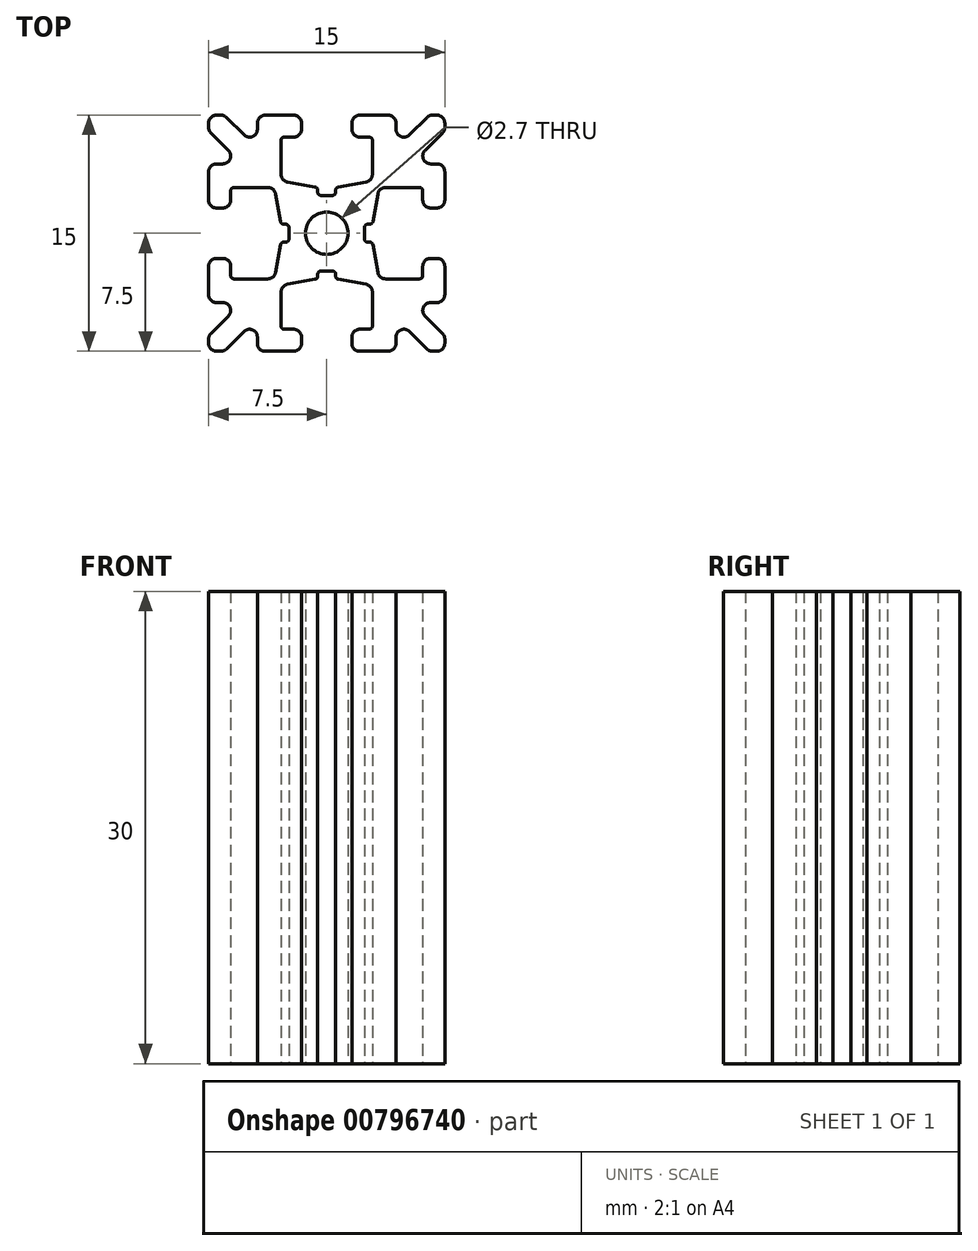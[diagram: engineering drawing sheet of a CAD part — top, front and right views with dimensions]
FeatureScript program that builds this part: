
annotation { "Feature Type Name" : "Feature", "Feature Type Description" : "" }
export const myFeature = defineFeature(function(context is Context, id is Id, definition is map)
    precondition{}
    {
        {
            var Q0;
            Q0=qCreatedBy(makeId("Top.planeOp"),FACE);
            var sketch = newSketch(context, id + "F0", { "sketchPlane" : qUnion([Q0])});
            skLineSegment(sketch, "E0", {"start": v(0, 0) * mm, "end": v(-7.5, -7.5) * mm, "construction": true});
            skArc(sketch, "E1", {"start": v(-1.35, 0) * mm, "mid": v(-1.25, -0.52) * mm, "end": v(-0.95, -0.95) * mm});
            skLineSegment(sketch, "E2", {"start": v(-7.5, -7) * mm, "end": v(-7.5, -6.72) * mm});
            skLineSegment(sketch, "E3", {"start": v(-7.35, -6.36) * mm, "end": v(-6.25, -5.26) * mm});
            skLineSegment(sketch, "E4", {"start": v(-6.6, -4.4) * mm, "end": v(-7, -4.4) * mm});
            skLineSegment(sketch, "E5", {"start": v(-7.5, -3.9) * mm, "end": v(-7.5, -2.1) * mm});
            skLineSegment(sketch, "E6", {"start": v(-7, -1.6) * mm, "end": v(-6.6, -1.6) * mm});
            skLineSegment(sketch, "E7", {"start": v(-6.1, -2.1) * mm, "end": v(-6.1, -2.7) * mm});
            skLineSegment(sketch, "E8", {"start": v(-5.9, -2.9) * mm, "end": v(-3.74, -2.9) * mm});
            skLineSegment(sketch, "E9", {"start": v(-3.25, -2.49) * mm, "end": v(-2.93, -0.73) * mm});
            skLineSegment(sketch, "E10", {"start": v(-2.73, -0.57) * mm, "end": v(-2.6, -0.57) * mm});
            skLineSegment(sketch, "E11", {"start": v(-2.4, -0.37) * mm, "end": v(-2.4, 0) * mm});
            skLineSegment(sketch, "E12", {"start": v(-2.4, 0) * mm, "end": v(-1.35, 0) * mm, "construction": true});
            skPoint(sketch, "E13.visualSharp", {"position": v(-5.4, -4.4) * mm});
            skArc(sketch, "E13.filletArc", {"start": v(-6.25, -5.26) * mm, "mid": v(-6.14, -4.71) * mm, "end": v(-6.6, -4.4) * mm});
            skPoint(sketch, "E14.visualSharp", {"position": v(-6.1, -2.9) * mm});
            skArc(sketch, "E14.filletArc", {"start": v(-6.1, -2.7) * mm, "mid": v(-6.04, -2.84) * mm, "end": v(-5.9, -2.9) * mm});
            skPoint(sketch, "E15.visualSharp", {"position": v(-6.1, -1.6) * mm});
            skArc(sketch, "E15.filletArc", {"start": v(-6.1, -2.1) * mm, "mid": v(-6.25, -1.75) * mm, "end": v(-6.6, -1.6) * mm});
            skPoint(sketch, "E16.visualSharp", {"position": v(-7.5, -1.6) * mm});
            skArc(sketch, "E16.filletArc", {"start": v(-7, -1.6) * mm, "mid": v(-7.35, -1.75) * mm, "end": v(-7.5, -2.1) * mm});
            skPoint(sketch, "E17.visualSharp", {"position": v(-7.5, -4.4) * mm});
            skArc(sketch, "E17.filletArc", {"start": v(-7.5, -3.9) * mm, "mid": v(-7.35, -4.26) * mm, "end": v(-7, -4.4) * mm});
            skPoint(sketch, "E18.visualSharp", {"position": v(-7.5, -6.51) * mm});
            skArc(sketch, "E18.filletArc", {"start": v(-7.35, -6.36) * mm, "mid": v(-7.46, -6.53) * mm, "end": v(-7.5, -6.72) * mm});
            skPoint(sketch, "E19.visualSharp", {"position": v(-3.32, -2.9) * mm});
            skArc(sketch, "E19.filletArc", {"start": v(-3.74, -2.9) * mm, "mid": v(-3.42, -2.78) * mm, "end": v(-3.25, -2.49) * mm});
            skPoint(sketch, "E20.visualSharp", {"position": v(-2.9, -0.57) * mm});
            skArc(sketch, "E20.filletArc", {"start": v(-2.73, -0.57) * mm, "mid": v(-2.86, -0.62) * mm, "end": v(-2.93, -0.73) * mm});
            skPoint(sketch, "E21.visualSharp", {"position": v(-2.4, -0.57) * mm});
            skArc(sketch, "E21.filletArc", {"start": v(-2.6, -0.57) * mm, "mid": v(-2.46, -0.51) * mm, "end": v(-2.4, -0.37) * mm});
            skLineSegment(sketch, "E22.0.MirrorCS", {"start": v(0, -2.4) * mm, "end": v(0, -1.35) * mm, "construction": true});
            skPoint(sketch, "E22.1.MirrorP", {"position": v(-4.4, -7.5) * mm});
            skArc(sketch, "E22.2.MirrorCS", {"start": v(-6.36, -7.35) * mm, "mid": v(-6.53, -7.46) * mm, "end": v(-6.72, -7.5) * mm});
            skPoint(sketch, "E22.3.MirrorP", {"position": v(-1.6, -7.5) * mm});
            skArc(sketch, "E22.4.MirrorCS", {"start": v(-1.6, -7) * mm, "mid": v(-1.75, -7.35) * mm, "end": v(-2.1, -7.5) * mm});
            skArc(sketch, "E22.5.MirrorCS", {"start": v(-0.57, -2.73) * mm, "mid": v(-0.62, -2.86) * mm, "end": v(-0.73, -2.93) * mm});
            skPoint(sketch, "E22.6.MirrorP", {"position": v(-1.6, -6.1) * mm});
            skLineSegment(sketch, "E22.7.MirrorCS", {"start": v(-3.9, -7.5) * mm, "end": v(-2.1, -7.5) * mm});
            skArc(sketch, "E22.8.MirrorCS", {"start": v(-5.26, -6.25) * mm, "mid": v(-4.71, -6.14) * mm, "end": v(-4.4, -6.6) * mm});
            skPoint(sketch, "E22.9.MirrorP", {"position": v(-0.57, -2.4) * mm});
            skPoint(sketch, "E22.10.MirrorP", {"position": v(-4.4, -5.4) * mm});
            skArc(sketch, "E22.11.MirrorCS", {"start": v(-2.7, -6.1) * mm, "mid": v(-2.84, -6.04) * mm, "end": v(-2.9, -5.9) * mm});
            skPoint(sketch, "E22.12.MirrorP", {"position": v(-0.57, -2.9) * mm});
            skLineSegment(sketch, "E22.13.MirrorCS", {"start": v(-7, -7.5) * mm, "end": v(-6.72, -7.5) * mm});
            skLineSegment(sketch, "E22.14.MirrorCS", {"start": v(-1.6, -7) * mm, "end": v(-1.6, -6.6) * mm});
            skLineSegment(sketch, "E22.15.MirrorCS", {"start": v(-6.36, -7.35) * mm, "end": v(-5.26, -6.25) * mm});
            skArc(sketch, "E22.16.MirrorCS", {"start": v(-2.1, -6.1) * mm, "mid": v(-1.75, -6.25) * mm, "end": v(-1.6, -6.6) * mm});
            skLineSegment(sketch, "E22.17.MirrorCS", {"start": v(-4.4, -6.6) * mm, "end": v(-4.4, -7) * mm});
            skArc(sketch, "E22.18.MirrorCS", {"start": v(-2.9, -3.74) * mm, "mid": v(-2.78, -3.42) * mm, "end": v(-2.49, -3.25) * mm});
            skLineSegment(sketch, "E22.19.MirrorCS", {"start": v(-2.9, -5.9) * mm, "end": v(-2.9, -3.74) * mm});
            skLineSegment(sketch, "E22.20.MirrorCS", {"start": v(-2.1, -6.1) * mm, "end": v(-2.7, -6.1) * mm});
            skArc(sketch, "E22.21.MirrorCS", {"start": v(-0.57, -2.6) * mm, "mid": v(-0.51, -2.46) * mm, "end": v(-0.37, -2.4) * mm});
            skLineSegment(sketch, "E22.22.MirrorCS", {"start": v(-0.37, -2.4) * mm, "end": v(0, -2.4) * mm});
            skPoint(sketch, "E22.23.MirrorP", {"position": v(-6.51, -7.5) * mm});
            skPoint(sketch, "E22.24.MirrorP", {"position": v(-2.9, -6.1) * mm});
            skLineSegment(sketch, "E22.25.MirrorCS", {"start": v(-2.49, -3.25) * mm, "end": v(-0.73, -2.93) * mm});
            skLineSegment(sketch, "E22.26.MirrorCS", {"start": v(-0.57, -2.73) * mm, "end": v(-0.57, -2.6) * mm});
            skArc(sketch, "E22.27.MirrorCS", {"start": v(0, -1.35) * mm, "mid": v(-0.52, -1.25) * mm, "end": v(-0.95, -0.95) * mm});
            skArc(sketch, "E22.28.MirrorCS", {"start": v(-3.9, -7.5) * mm, "mid": v(-4.26, -7.35) * mm, "end": v(-4.4, -7) * mm});
            skPoint(sketch, "E22.29.MirrorP", {"position": v(-2.9, -3.32) * mm});
            skPoint(sketch, "E23.visualSharp", {"position": v(-7.5, -7.5) * mm});
            skArc(sketch, "E23.filletArc", {"start": v(-7.5, -7) * mm, "mid": v(-7.35, -7.35) * mm, "end": v(-7, -7.5) * mm});
            skLineSegment(sketch, "E24.0.MirrorCS", {"start": v(0, 2.4) * mm, "end": v(0, 1.35) * mm, "construction": true});
            skLineSegment(sketch, "E24.1.MirrorCS", {"start": v(-2.1, 6.1) * mm, "end": v(-2.7, 6.1) * mm});
            skLineSegment(sketch, "E24.2.MirrorCS", {"start": v(-7.5, 3.9) * mm, "end": v(-7.5, 2.1) * mm});
            skLineSegment(sketch, "E24.3.MirrorCS", {"start": v(-7, 1.6) * mm, "end": v(-6.6, 1.6) * mm});
            skArc(sketch, "E24.4.MirrorCS", {"start": v(-6.1, 2.1) * mm, "mid": v(-6.25, 1.75) * mm, "end": v(-6.6, 1.6) * mm});
            skPoint(sketch, "E24.5.MirrorP", {"position": v(-3.32, 2.9) * mm});
            skPoint(sketch, "E24.6.MirrorP", {"position": v(-0.57, 2.9) * mm});
            skArc(sketch, "E24.7.MirrorCS", {"start": v(-0.57, 2.6) * mm, "mid": v(-0.51, 2.46) * mm, "end": v(-0.37, 2.4) * mm});
            skArc(sketch, "E24.8.MirrorCS", {"start": v(-2.6, 0.57) * mm, "mid": v(-2.46, 0.51) * mm, "end": v(-2.4, 0.37) * mm});
            skLineSegment(sketch, "E24.9.MirrorCS", {"start": v(-0.37, 2.4) * mm, "end": v(0, 2.4) * mm});
            skArc(sketch, "E24.10.MirrorCS", {"start": v(-6.1, 2.7) * mm, "mid": v(-6.04, 2.84) * mm, "end": v(-5.9, 2.9) * mm});
            skPoint(sketch, "E24.11.MirrorP", {"position": v(-4.4, 5.4) * mm});
            skLineSegment(sketch, "E24.12.MirrorCS", {"start": v(-2.9, 5.9) * mm, "end": v(-2.9, 3.74) * mm});
            skLineSegment(sketch, "E24.13.MirrorCS", {"start": v(-7.35, 6.36) * mm, "end": v(-6.25, 5.26) * mm});
            skPoint(sketch, "E24.14.MirrorP", {"position": v(-7.5, 6.51) * mm});
            skArc(sketch, "E24.15.MirrorCS", {"start": v(-3.74, 2.9) * mm, "mid": v(-3.42, 2.78) * mm, "end": v(-3.25, 2.49) * mm});
            skArc(sketch, "E24.16.MirrorCS", {"start": v(-2.1, 6.1) * mm, "mid": v(-1.75, 6.25) * mm, "end": v(-1.6, 6.6) * mm});
            skArc(sketch, "E24.17.MirrorCS", {"start": v(-7, 1.6) * mm, "mid": v(-7.35, 1.75) * mm, "end": v(-7.5, 2.1) * mm});
            skPoint(sketch, "E24.18.MirrorP", {"position": v(-1.6, 6.1) * mm});
            skPoint(sketch, "E24.19.MirrorP", {"position": v(-7.5, 4.4) * mm});
            skLineSegment(sketch, "E24.20.MirrorCS", {"start": v(-4.4, 6.6) * mm, "end": v(-4.4, 7) * mm});
            skArc(sketch, "E24.21.MirrorCS", {"start": v(-7.5, 3.9) * mm, "mid": v(-7.35, 4.26) * mm, "end": v(-7, 4.4) * mm});
            skPoint(sketch, "E24.22.MirrorP", {"position": v(-0.57, 2.4) * mm});
            skLineSegment(sketch, "E24.23.MirrorCS", {"start": v(-5.9, 2.9) * mm, "end": v(-3.74, 2.9) * mm});
            skArc(sketch, "E24.24.MirrorCS", {"start": v(-2.9, 3.74) * mm, "mid": v(-2.78, 3.42) * mm, "end": v(-2.49, 3.25) * mm});
            skArc(sketch, "E24.25.MirrorCS", {"start": v(-7.35, 6.36) * mm, "mid": v(-7.46, 6.53) * mm, "end": v(-7.5, 6.72) * mm});
            skPoint(sketch, "E24.26.MirrorP", {"position": v(-6.1, 2.9) * mm});
            skPoint(sketch, "E24.27.MirrorP", {"position": v(-4.4, 7.5) * mm});
            skArc(sketch, "E24.28.MirrorCS", {"start": v(-5.26, 6.25) * mm, "mid": v(-4.71, 6.14) * mm, "end": v(-4.4, 6.6) * mm});
            skArc(sketch, "E24.29.MirrorCS", {"start": v(-7.5, 7) * mm, "mid": v(-7.35, 7.35) * mm, "end": v(-7, 7.5) * mm});
            skPoint(sketch, "E24.30.MirrorP", {"position": v(-6.1, 1.6) * mm});
            skPoint(sketch, "E24.31.MirrorP", {"position": v(-2.9, 3.32) * mm});
            skPoint(sketch, "E24.32.MirrorP", {"position": v(-1.6, 7.5) * mm});
            skPoint(sketch, "E24.33.MirrorP", {"position": v(-2.9, 6.1) * mm});
            skLineSegment(sketch, "E24.34.MirrorCS", {"start": v(-3.9, 7.5) * mm, "end": v(-2.1, 7.5) * mm});
            skLineSegment(sketch, "E24.35.MirrorCS", {"start": v(-7, 7.5) * mm, "end": v(-6.72, 7.5) * mm});
            skArc(sketch, "E24.36.MirrorCS", {"start": v(-3.9, 7.5) * mm, "mid": v(-4.26, 7.35) * mm, "end": v(-4.4, 7) * mm});
            skPoint(sketch, "E24.37.MirrorP", {"position": v(-7.5, 7.5) * mm});
            skLineSegment(sketch, "E24.38.MirrorCS", {"start": v(-1.6, 7) * mm, "end": v(-1.6, 6.6) * mm});
            skLineSegment(sketch, "E24.39.MirrorCS", {"start": v(-6.36, 7.35) * mm, "end": v(-5.26, 6.25) * mm});
            skPoint(sketch, "E24.40.MirrorP", {"position": v(-7.5, 1.6) * mm});
            skArc(sketch, "E24.41.MirrorCS", {"start": v(-2.7, 6.1) * mm, "mid": v(-2.84, 6.04) * mm, "end": v(-2.9, 5.9) * mm});
            skArc(sketch, "E24.42.MirrorCS", {"start": v(-6.36, 7.35) * mm, "mid": v(-6.53, 7.46) * mm, "end": v(-6.72, 7.5) * mm});
            skLineSegment(sketch, "E24.43.MirrorCS", {"start": v(-2.49, 3.25) * mm, "end": v(-0.73, 2.93) * mm});
            skPoint(sketch, "E24.44.MirrorP", {"position": v(-2.9, 0.57) * mm});
            skLineSegment(sketch, "E24.45.MirrorCS", {"start": v(-6.6, 4.4) * mm, "end": v(-7, 4.4) * mm});
            skArc(sketch, "E24.46.MirrorCS", {"start": v(-1.6, 7) * mm, "mid": v(-1.75, 7.35) * mm, "end": v(-2.1, 7.5) * mm});
            skArc(sketch, "E24.47.MirrorCS", {"start": v(-2.73, 0.57) * mm, "mid": v(-2.86, 0.62) * mm, "end": v(-2.93, 0.73) * mm});
            skArc(sketch, "E24.48.MirrorCS", {"start": v(-6.25, 5.26) * mm, "mid": v(-6.14, 4.71) * mm, "end": v(-6.6, 4.4) * mm});
            skLineSegment(sketch, "E24.49.MirrorCS", {"start": v(-0.57, 2.73) * mm, "end": v(-0.57, 2.6) * mm});
            skLineSegment(sketch, "E24.50.MirrorCS", {"start": v(-2.73, 0.57) * mm, "end": v(-2.6, 0.57) * mm});
            skArc(sketch, "E24.51.MirrorCS", {"start": v(-1.35, 0) * mm, "mid": v(-1.25, 0.52) * mm, "end": v(-0.95, 0.95) * mm});
            skPoint(sketch, "E24.52.MirrorP", {"position": v(-2.4, 0.57) * mm});
            skPoint(sketch, "E24.53.MirrorP", {"position": v(-5.4, 4.4) * mm});
            skLineSegment(sketch, "E24.54.MirrorCS", {"start": v(-2.4, 0.37) * mm, "end": v(-2.4, 0) * mm});
            skArc(sketch, "E24.55.MirrorCS", {"start": v(0, 1.35) * mm, "mid": v(-0.52, 1.25) * mm, "end": v(-0.95, 0.95) * mm});
            skLineSegment(sketch, "E24.56.MirrorCS", {"start": v(-3.25, 2.49) * mm, "end": v(-2.93, 0.73) * mm});
            skLineSegment(sketch, "E24.57.MirrorCS", {"start": v(-6.1, 2.1) * mm, "end": v(-6.1, 2.7) * mm});
            skLineSegment(sketch, "E24.58.MirrorCS", {"start": v(-7.5, 7) * mm, "end": v(-7.5, 6.72) * mm});
            skArc(sketch, "E24.59.MirrorCS", {"start": v(-0.57, 2.73) * mm, "mid": v(-0.62, 2.86) * mm, "end": v(-0.73, 2.93) * mm});
            skPoint(sketch, "E24.60.MirrorP", {"position": v(-6.51, 7.5) * mm});
            skLineSegment(sketch, "E25.0.MirrorCS", {"start": v(7, -7.5) * mm, "end": v(6.72, -7.5) * mm});
            skLineSegment(sketch, "E25.1.MirrorCS", {"start": v(0.57, 2.73) * mm, "end": v(0.57, 2.6) * mm});
            skLineSegment(sketch, "E25.2.MirrorCS", {"start": v(0.37, 2.4) * mm, "end": v(0, 2.4) * mm});
            skLineSegment(sketch, "E25.3.MirrorCS", {"start": v(7, 7.5) * mm, "end": v(6.72, 7.5) * mm});
            skLineSegment(sketch, "E25.4.MirrorCS", {"start": v(1.6, -7) * mm, "end": v(1.6, -6.6) * mm});
            skLineSegment(sketch, "E25.5.MirrorCS", {"start": v(2.73, 0.57) * mm, "end": v(2.6, 0.57) * mm});
            skLineSegment(sketch, "E25.6.MirrorCS", {"start": v(7, 1.6) * mm, "end": v(6.6, 1.6) * mm});
            skLineSegment(sketch, "E25.7.MirrorCS", {"start": v(5.9, 2.9) * mm, "end": v(3.74, 2.9) * mm});
            skLineSegment(sketch, "E25.8.MirrorCS", {"start": v(7.35, 6.36) * mm, "end": v(6.25, 5.26) * mm});
            skArc(sketch, "E25.9.MirrorCS", {"start": v(2.7, -6.1) * mm, "mid": v(2.84, -6.04) * mm, "end": v(2.9, -5.9) * mm});
            skArc(sketch, "E25.10.MirrorCS", {"start": v(2.9, 3.74) * mm, "mid": v(2.78, 3.42) * mm, "end": v(2.49, 3.25) * mm});
            skPoint(sketch, "E25.11.MirrorP", {"position": v(1.6, -7.5) * mm});
            skPoint(sketch, "E25.12.MirrorP", {"position": v(6.1, -1.6) * mm});
            skPoint(sketch, "E25.13.MirrorP", {"position": v(2.9, 3.32) * mm});
            skPoint(sketch, "E25.14.MirrorP", {"position": v(7.5, -1.6) * mm});
            skArc(sketch, "E25.15.MirrorCS", {"start": v(1.6, 7) * mm, "mid": v(1.75, 7.35) * mm, "end": v(2.1, 7.5) * mm});
            skLineSegment(sketch, "E25.16.MirrorCS", {"start": v(6.1, -2.1) * mm, "end": v(6.1, -2.7) * mm});
            skLineSegment(sketch, "E25.17.MirrorCS", {"start": v(2.4, 0.37) * mm, "end": v(2.4, 0) * mm});
            skArc(sketch, "E25.18.MirrorCS", {"start": v(7, -1.6) * mm, "mid": v(7.35, -1.75) * mm, "end": v(7.5, -2.1) * mm});
            skArc(sketch, "E25.19.MirrorCS", {"start": v(7.5, 7) * mm, "mid": v(7.35, 7.35) * mm, "end": v(7, 7.5) * mm});
            skArc(sketch, "E25.20.MirrorCS", {"start": v(2.1, -6.1) * mm, "mid": v(1.75, -6.25) * mm, "end": v(1.6, -6.6) * mm});
            skArc(sketch, "E25.21.MirrorCS", {"start": v(6.1, 2.1) * mm, "mid": v(6.25, 1.75) * mm, "end": v(6.6, 1.6) * mm});
            skLineSegment(sketch, "E25.22.MirrorCS", {"start": v(4.4, 6.6) * mm, "end": v(4.4, 7) * mm});
            skLineSegment(sketch, "E25.23.MirrorCS", {"start": v(6.6, 4.4) * mm, "end": v(7, 4.4) * mm});
            skArc(sketch, "E25.24.MirrorCS", {"start": v(7, 1.6) * mm, "mid": v(7.35, 1.75) * mm, "end": v(7.5, 2.1) * mm});
            skArc(sketch, "E25.25.MirrorCS", {"start": v(0, -1.35) * mm, "mid": v(0.52, -1.25) * mm, "end": v(0.95, -0.95) * mm});
            skLineSegment(sketch, "E25.26.MirrorCS", {"start": v(3.9, -7.5) * mm, "end": v(2.1, -7.5) * mm});
            skLineSegment(sketch, "E25.27.MirrorCS", {"start": v(2.1, 6.1) * mm, "end": v(2.7, 6.1) * mm});
            skLineSegment(sketch, "E25.28.MirrorCS", {"start": v(2.73, -0.57) * mm, "end": v(2.6, -0.57) * mm});
            skLineSegment(sketch, "E25.29.MirrorCS", {"start": v(4.4, -6.6) * mm, "end": v(4.4, -7) * mm});
            skLineSegment(sketch, "E25.30.MirrorCS", {"start": v(3.9, 7.5) * mm, "end": v(2.1, 7.5) * mm});
            skArc(sketch, "E25.31.MirrorCS", {"start": v(0.57, -2.73) * mm, "mid": v(0.62, -2.86) * mm, "end": v(0.73, -2.93) * mm});
            skArc(sketch, "E25.32.MirrorCS", {"start": v(0.57, 2.6) * mm, "mid": v(0.51, 2.46) * mm, "end": v(0.37, 2.4) * mm});
            skPoint(sketch, "E25.33.MirrorP", {"position": v(6.51, -7.5) * mm});
            skArc(sketch, "E25.34.MirrorCS", {"start": v(3.9, -7.5) * mm, "mid": v(4.26, -7.35) * mm, "end": v(4.4, -7) * mm});
            skArc(sketch, "E25.35.MirrorCS", {"start": v(2.7, 6.1) * mm, "mid": v(2.84, 6.04) * mm, "end": v(2.9, 5.9) * mm});
            skPoint(sketch, "E25.36.MirrorP", {"position": v(0.57, -2.4) * mm});
            skPoint(sketch, "E25.37.MirrorP", {"position": v(0.57, 2.9) * mm});
            skLineSegment(sketch, "E25.38.MirrorCS", {"start": v(3.25, -2.49) * mm, "end": v(2.93, -0.73) * mm});
            skPoint(sketch, "E25.39.MirrorP", {"position": v(5.4, -4.4) * mm});
            skPoint(sketch, "E25.40.MirrorP", {"position": v(2.4, -0.57) * mm});
            skLineSegment(sketch, "E25.41.MirrorCS", {"start": v(7.5, -7) * mm, "end": v(7.5, -6.72) * mm});
            skArc(sketch, "E25.42.MirrorCS", {"start": v(7.35, 6.36) * mm, "mid": v(7.46, 6.53) * mm, "end": v(7.5, 6.72) * mm});
            skPoint(sketch, "E25.43.MirrorP", {"position": v(4.4, 7.5) * mm});
            skArc(sketch, "E25.44.MirrorCS", {"start": v(6.25, 5.26) * mm, "mid": v(6.14, 4.71) * mm, "end": v(6.6, 4.4) * mm});
            skPoint(sketch, "E25.45.MirrorP", {"position": v(6.1, -2.9) * mm});
            skPoint(sketch, "E25.46.MirrorP", {"position": v(4.4, -7.5) * mm});
            skArc(sketch, "E25.47.MirrorCS", {"start": v(6.1, 2.7) * mm, "mid": v(6.04, 2.84) * mm, "end": v(5.9, 2.9) * mm});
            skLineSegment(sketch, "E25.48.MirrorCS", {"start": v(2.1, -6.1) * mm, "end": v(2.7, -6.1) * mm});
            skArc(sketch, "E25.49.MirrorCS", {"start": v(2.73, -0.57) * mm, "mid": v(2.86, -0.62) * mm, "end": v(2.93, -0.73) * mm});
            skArc(sketch, "E25.50.MirrorCS", {"start": v(7.35, -6.36) * mm, "mid": v(7.46, -6.53) * mm, "end": v(7.5, -6.72) * mm});
            skLineSegment(sketch, "E25.51.MirrorCS", {"start": v(3.25, 2.49) * mm, "end": v(2.93, 0.73) * mm});
            skArc(sketch, "E25.52.MirrorCS", {"start": v(2.9, -3.74) * mm, "mid": v(2.78, -3.42) * mm, "end": v(2.49, -3.25) * mm});
            skArc(sketch, "E25.53.MirrorCS", {"start": v(2.6, 0.57) * mm, "mid": v(2.46, 0.51) * mm, "end": v(2.4, 0.37) * mm});
            skPoint(sketch, "E25.54.MirrorP", {"position": v(2.9, 0.57) * mm});
            skPoint(sketch, "E25.55.MirrorP", {"position": v(7.5, -6.51) * mm});
            skLineSegment(sketch, "E25.56.MirrorCS", {"start": v(2.49, 3.25) * mm, "end": v(0.73, 2.93) * mm});
            skArc(sketch, "E25.57.MirrorCS", {"start": v(1.6, -7) * mm, "mid": v(1.75, -7.35) * mm, "end": v(2.1, -7.5) * mm});
            skArc(sketch, "E25.58.MirrorCS", {"start": v(2.1, 6.1) * mm, "mid": v(1.75, 6.25) * mm, "end": v(1.6, 6.6) * mm});
            skLineSegment(sketch, "E25.59.MirrorCS", {"start": v(0.57, -2.73) * mm, "end": v(0.57, -2.6) * mm});
            skLineSegment(sketch, "E25.60.MirrorCS", {"start": v(2.4, -0.37) * mm, "end": v(2.4, 0) * mm});
            skArc(sketch, "E25.61.MirrorCS", {"start": v(7.5, -3.9) * mm, "mid": v(7.35, -4.26) * mm, "end": v(7, -4.4) * mm});
            skLineSegment(sketch, "E25.62.MirrorCS", {"start": v(5.9, -2.9) * mm, "end": v(3.74, -2.9) * mm});
            skLineSegment(sketch, "E25.63.MirrorCS", {"start": v(7.5, -3.9) * mm, "end": v(7.5, -2.1) * mm});
            skLineSegment(sketch, "E25.64.MirrorCS", {"start": v(7, -1.6) * mm, "end": v(6.6, -1.6) * mm});
            skArc(sketch, "E25.65.MirrorCS", {"start": v(1.35, 0) * mm, "mid": v(1.25, -0.52) * mm, "end": v(0.95, -0.95) * mm});
            skPoint(sketch, "E25.66.MirrorP", {"position": v(7.5, 1.6) * mm});
            skPoint(sketch, "E25.67.MirrorP", {"position": v(1.6, 6.1) * mm});
            skLineSegment(sketch, "E25.68.MirrorCS", {"start": v(6.36, -7.35) * mm, "end": v(5.26, -6.25) * mm});
            skPoint(sketch, "E25.69.MirrorP", {"position": v(2.4, 0.57) * mm});
            skPoint(sketch, "E25.70.MirrorP", {"position": v(6.1, 1.6) * mm});
            skPoint(sketch, "E25.71.MirrorP", {"position": v(3.32, -2.9) * mm});
            skPoint(sketch, "E25.72.MirrorP", {"position": v(0.57, -2.9) * mm});
            skPoint(sketch, "E25.73.MirrorP", {"position": v(7.5, 4.4) * mm});
            skArc(sketch, "E25.74.MirrorCS", {"start": v(5.26, -6.25) * mm, "mid": v(4.71, -6.14) * mm, "end": v(4.4, -6.6) * mm});
            skArc(sketch, "E25.75.MirrorCS", {"start": v(7.5, -7) * mm, "mid": v(7.35, -7.35) * mm, "end": v(7, -7.5) * mm});
            skLineSegment(sketch, "E25.76.MirrorCS", {"start": v(2.49, -3.25) * mm, "end": v(0.73, -2.93) * mm});
            skArc(sketch, "E25.77.MirrorCS", {"start": v(3.74, 2.9) * mm, "mid": v(3.42, 2.78) * mm, "end": v(3.25, 2.49) * mm});
            skArc(sketch, "E25.78.MirrorCS", {"start": v(6.36, -7.35) * mm, "mid": v(6.53, -7.46) * mm, "end": v(6.72, -7.5) * mm});
            skArc(sketch, "E25.79.MirrorCS", {"start": v(7.5, 3.9) * mm, "mid": v(7.35, 4.26) * mm, "end": v(7, 4.4) * mm});
            skArc(sketch, "E25.80.MirrorCS", {"start": v(2.73, 0.57) * mm, "mid": v(2.86, 0.62) * mm, "end": v(2.93, 0.73) * mm});
            skArc(sketch, "E25.81.MirrorCS", {"start": v(6.36, 7.35) * mm, "mid": v(6.53, 7.46) * mm, "end": v(6.72, 7.5) * mm});
            skPoint(sketch, "E25.82.MirrorP", {"position": v(4.4, -5.4) * mm});
            skPoint(sketch, "E25.83.MirrorP", {"position": v(6.51, 7.5) * mm});
            skPoint(sketch, "E25.84.MirrorP", {"position": v(2.9, -0.57) * mm});
            skLineSegment(sketch, "E25.85.MirrorCS", {"start": v(2.9, -5.9) * mm, "end": v(2.9, -3.74) * mm});
            skLineSegment(sketch, "E25.86.MirrorCS", {"start": v(6.1, 2.1) * mm, "end": v(6.1, 2.7) * mm});
            skLineSegment(sketch, "E25.87.MirrorCS", {"start": v(6.36, 7.35) * mm, "end": v(5.26, 6.25) * mm});
            skArc(sketch, "E25.88.MirrorCS", {"start": v(0.57, 2.73) * mm, "mid": v(0.62, 2.86) * mm, "end": v(0.73, 2.93) * mm});
            skArc(sketch, "E25.89.MirrorCS", {"start": v(0.57, -2.6) * mm, "mid": v(0.51, -2.46) * mm, "end": v(0.37, -2.4) * mm});
            skLineSegment(sketch, "E25.90.MirrorCS", {"start": v(2.9, 5.9) * mm, "end": v(2.9, 3.74) * mm});
            skArc(sketch, "E25.91.MirrorCS", {"start": v(0, 1.35) * mm, "mid": v(0.52, 1.25) * mm, "end": v(0.95, 0.95) * mm});
            skArc(sketch, "E25.92.MirrorCS", {"start": v(2.6, -0.57) * mm, "mid": v(2.46, -0.51) * mm, "end": v(2.4, -0.37) * mm});
            skPoint(sketch, "E25.93.MirrorP", {"position": v(4.4, 5.4) * mm});
            skPoint(sketch, "E25.94.MirrorP", {"position": v(2.9, -3.32) * mm});
            skPoint(sketch, "E25.95.MirrorP", {"position": v(2.9, 6.1) * mm});
            skPoint(sketch, "E25.96.MirrorP", {"position": v(5.4, 4.4) * mm});
            skPoint(sketch, "E25.97.MirrorP", {"position": v(3.32, 2.9) * mm});
            skArc(sketch, "E25.98.MirrorCS", {"start": v(3.74, -2.9) * mm, "mid": v(3.42, -2.78) * mm, "end": v(3.25, -2.49) * mm});
            skArc(sketch, "E25.99.MirrorCS", {"start": v(3.9, 7.5) * mm, "mid": v(4.26, 7.35) * mm, "end": v(4.4, 7) * mm});
            skPoint(sketch, "E25.100.MirrorP", {"position": v(7.5, -4.4) * mm});
            skPoint(sketch, "E25.101.MirrorP", {"position": v(6.1, 2.9) * mm});
            skArc(sketch, "E25.102.MirrorCS", {"start": v(1.35, 0) * mm, "mid": v(1.25, 0.52) * mm, "end": v(0.95, 0.95) * mm});
            skArc(sketch, "E25.103.MirrorCS", {"start": v(5.26, 6.25) * mm, "mid": v(4.71, 6.14) * mm, "end": v(4.4, 6.6) * mm});
            skPoint(sketch, "E25.104.MirrorP", {"position": v(7.5, 6.51) * mm});
            skPoint(sketch, "E25.105.MirrorP", {"position": v(2.9, -6.1) * mm});
            skArc(sketch, "E25.106.MirrorCS", {"start": v(6.25, -5.26) * mm, "mid": v(6.14, -4.71) * mm, "end": v(6.6, -4.4) * mm});
            skArc(sketch, "E25.107.MirrorCS", {"start": v(6.1, -2.1) * mm, "mid": v(6.25, -1.75) * mm, "end": v(6.6, -1.6) * mm});
            skPoint(sketch, "E25.108.MirrorP", {"position": v(1.6, 7.5) * mm});
            skPoint(sketch, "E25.109.MirrorP", {"position": v(7.5, 7.5) * mm});
            skLineSegment(sketch, "E25.110.MirrorCS", {"start": v(0.37, -2.4) * mm, "end": v(0, -2.4) * mm});
            skPoint(sketch, "E25.111.MirrorP", {"position": v(7.5, -7.5) * mm});
            skLineSegment(sketch, "E25.112.MirrorCS", {"start": v(7.5, 7) * mm, "end": v(7.5, 6.72) * mm});
            skArc(sketch, "E25.113.MirrorCS", {"start": v(6.1, -2.7) * mm, "mid": v(6.04, -2.84) * mm, "end": v(5.9, -2.9) * mm});
            skLineSegment(sketch, "E25.114.MirrorCS", {"start": v(1.6, 7) * mm, "end": v(1.6, 6.6) * mm});
            skPoint(sketch, "E25.115.MirrorP", {"position": v(1.6, -6.1) * mm});
            skLineSegment(sketch, "E25.116.MirrorCS", {"start": v(7.35, -6.36) * mm, "end": v(6.25, -5.26) * mm});
            skLineSegment(sketch, "E25.117.MirrorCS", {"start": v(7.5, 3.9) * mm, "end": v(7.5, 2.1) * mm});
            skPoint(sketch, "E25.118.MirrorP", {"position": v(0.57, 2.4) * mm});
            skLineSegment(sketch, "E25.119.MirrorCS", {"start": v(6.6, -4.4) * mm, "end": v(7, -4.4) * mm});
            skSolve(sketch);
        }
        {
            var Q0;
            Q0=makeQuery(id+"F0.imprint","IMPRINT",FACE,{"disambiguationData":[TD([[makeQuery(id+"F0.imprint","IMPRINT",EDGE,{"derivedFrom":sQuery(id+"F0.wireOp",EDGE,"E1")}),-1.0]])]});
            extrude(context, id + "F1", {"entities" : qUnion([Q0]), "depth" : 30 * mm, "offsetDistance" : 25 * mm});
        }
    });
